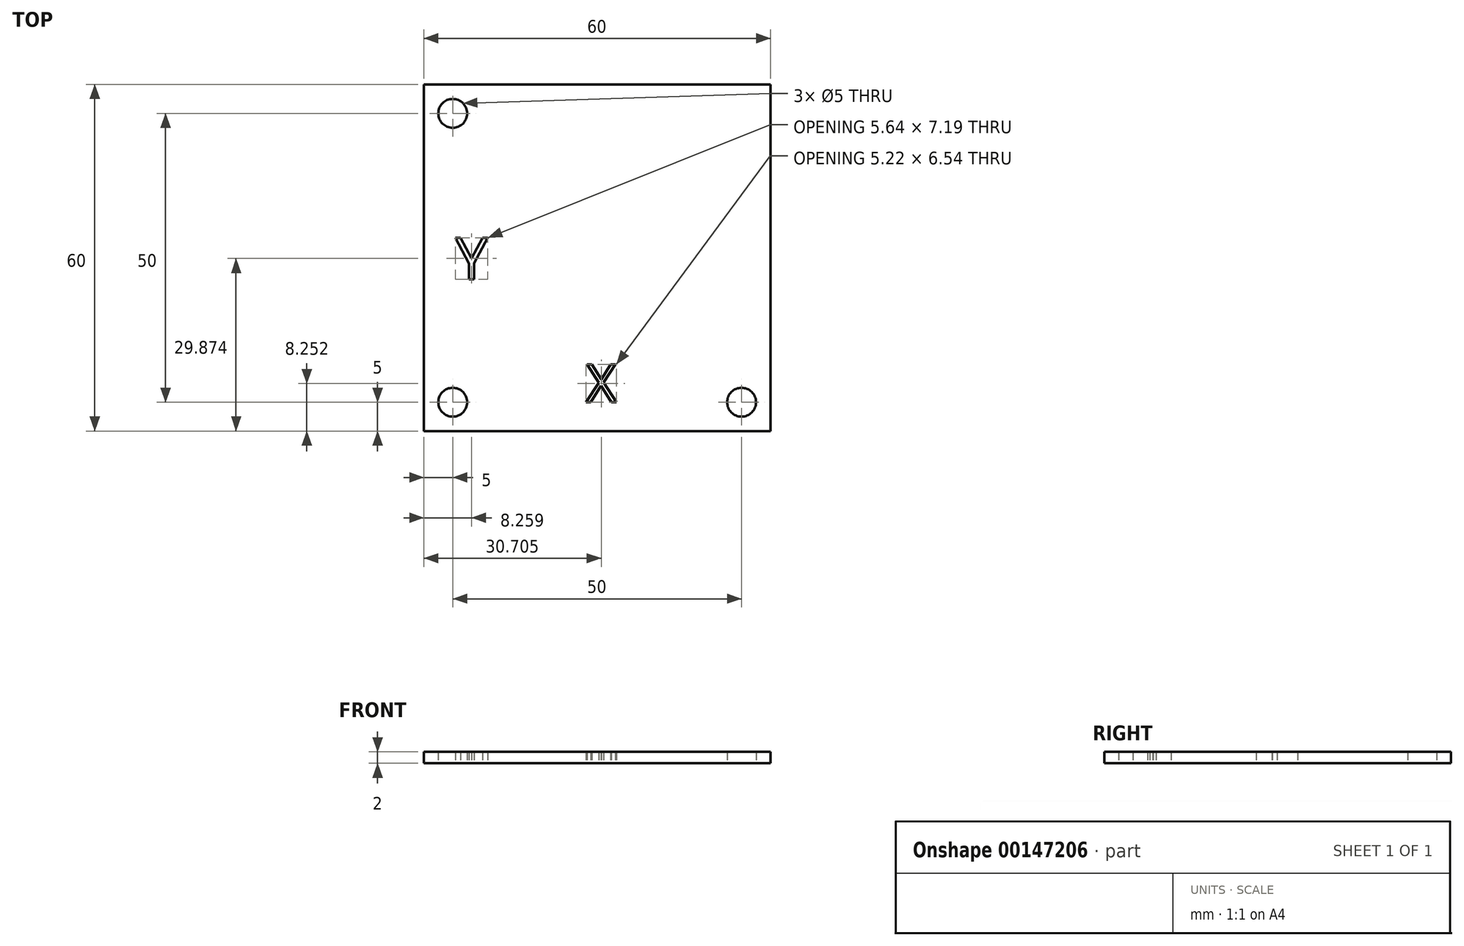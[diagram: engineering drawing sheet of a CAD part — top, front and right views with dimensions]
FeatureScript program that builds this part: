
annotation { "Feature Type Name" : "Feature", "Feature Type Description" : "" }
export const myFeature = defineFeature(function(context is Context, id is Id, definition is map)
    precondition{}
    {
        {
            var Q0;
            Q0=qCreatedBy(makeId("Top.planeOp"),FACE);
            var sketch = newSketch(context, id + "F0", { "sketchPlane" : qUnion([Q0])});
            skLineSegment(sketch, "E0.bottom", {"start": v(0, 0) * mm, "end": v(60, 0) * mm});
            skLineSegment(sketch, "E0.top", {"start": v(0, -60) * mm, "end": v(60, -60) * mm});
            skLineSegment(sketch, "E0.left", {"start": v(0, 0) * mm, "end": v(0, -60) * mm});
            skLineSegment(sketch, "E0.right", {"start": v(60, 0) * mm, "end": v(60, -60) * mm});
            skCircle(sketch, "E1", {"center": v(5, -5) * mm, "radius": 2.5 * mm});
            skCircle(sketch, "E2", {"center": v(5, -55) * mm, "radius": 2.5 * mm});
            skCircle(sketch, "E3", {"center": v(55, -55) * mm, "radius": 2.5 * mm});
            skText(sketch, "E4", { "text": "Y\n", "fontName": "OpenSans-Regular.ttf"});
            skText(sketch, "E5", { "text": "X\n", "fontName": "OpenSans-Regular.ttf"});
            const initialGuessF0  = {"E4": [0.00544, -0.03372, 1, 0, 0.00725], "E5": [0.02806, -0.05502, 1, 0, 0.0066]};
            skSetInitialGuess(sketch, initialGuessF0);
            skSolve(sketch);
        }
        {
            var Q0;
            Q0 = qSketchRegion(id + "F0", true);
            extrude(context, id + "F1", {"entities" : qUnion([Q0]), "depth" : 2 * mm});
        }
    });
